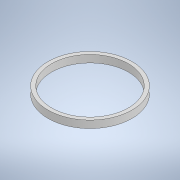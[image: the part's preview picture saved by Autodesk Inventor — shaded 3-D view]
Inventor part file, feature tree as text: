
AUTODESK INVENTOR PART (.ipt)
format: ipt  version: 2022.3 (Build 263350000, 350)  size: 102,400 bytes
history: native  units: mm
features: extrude x1, sketch x1
ambient origin geometry x8: Origin, YZ Plane, XZ Plane, XY Plane, X Axis, Y Axis, Z Axis, Center Point
bodies: Solid1 (feature_tree)
feature tree (2):
  extrude  "Extrusion1"  Depth=4.0mm
  sketch  "Sketch1"  dims[d0=42.0mm d1=2.0mm d2=4.0mm d3=0.0mm]
